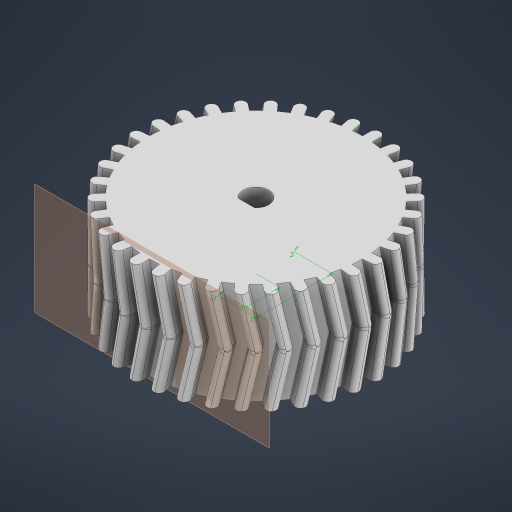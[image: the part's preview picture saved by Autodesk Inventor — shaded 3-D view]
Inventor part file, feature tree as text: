
AUTODESK INVENTOR PART (.ipt)
format: ipt  version: 2023 (Build 270158030, 158C)  size: 750,592 bytes
history: native  units: in
note: dims shown in document units (in); Inventor stores cm internally (conversion verified against a paired STEP export)
features: sketch x5, extrude x4, plane x1, fillet x1, pattern_circular x1
ambient origin geometry x8: Origin, YZ Plane, XZ Plane, XY Plane, X Axis, Y Axis, Z Axis, Center Point
bodies: Solid1 (feature_tree)
feature tree (12):
  extrude  "Extrusion1"  Depth=0.7874in TaperAngle=0.0deg
  plane  "Work Plane1"
  extrude  "Extrusion2"  Depth=0.8071in
  extrude  "Extrusion3"  Depth=0.0787in
  fillet  "Fillet3"  Radius=0.1181in
  pattern_circular  "Circular Pattern2"  [2 undecoded]
  extrude  "Extrusion5"  Depth=0.0394in
  sketch  "Sketch14"  dims[d18=0.1732in d19=0.8268in d20=0.0in d23=0.0394in d24=13.189in d25=360.0deg d30=0.874in d31=0.2756in d32=0.0in d33=0.1181in d34=0.1181in d35=0.5906in d37=0.2953in d26=0.0in]
  sketch  "Sketch3"  dims[d0=1.6535in d1=0.7874in d2=0.0in]
  sketch  "Sketch8"  dims[d3=0.8071in d4=0.0787in]
  sketch  "Sketch10"  dims[d5=0.0787in d6=0.0787in d7=0.1181in d8=0.0in]
  sketch  "Sketch13"  dims[d17=0.1969in]
note: 2 required parameter values undecoded (feature->parameter linkage not recoverable at this tier; creation-order binding heuristic only, values carry confidence <= 0.55)
